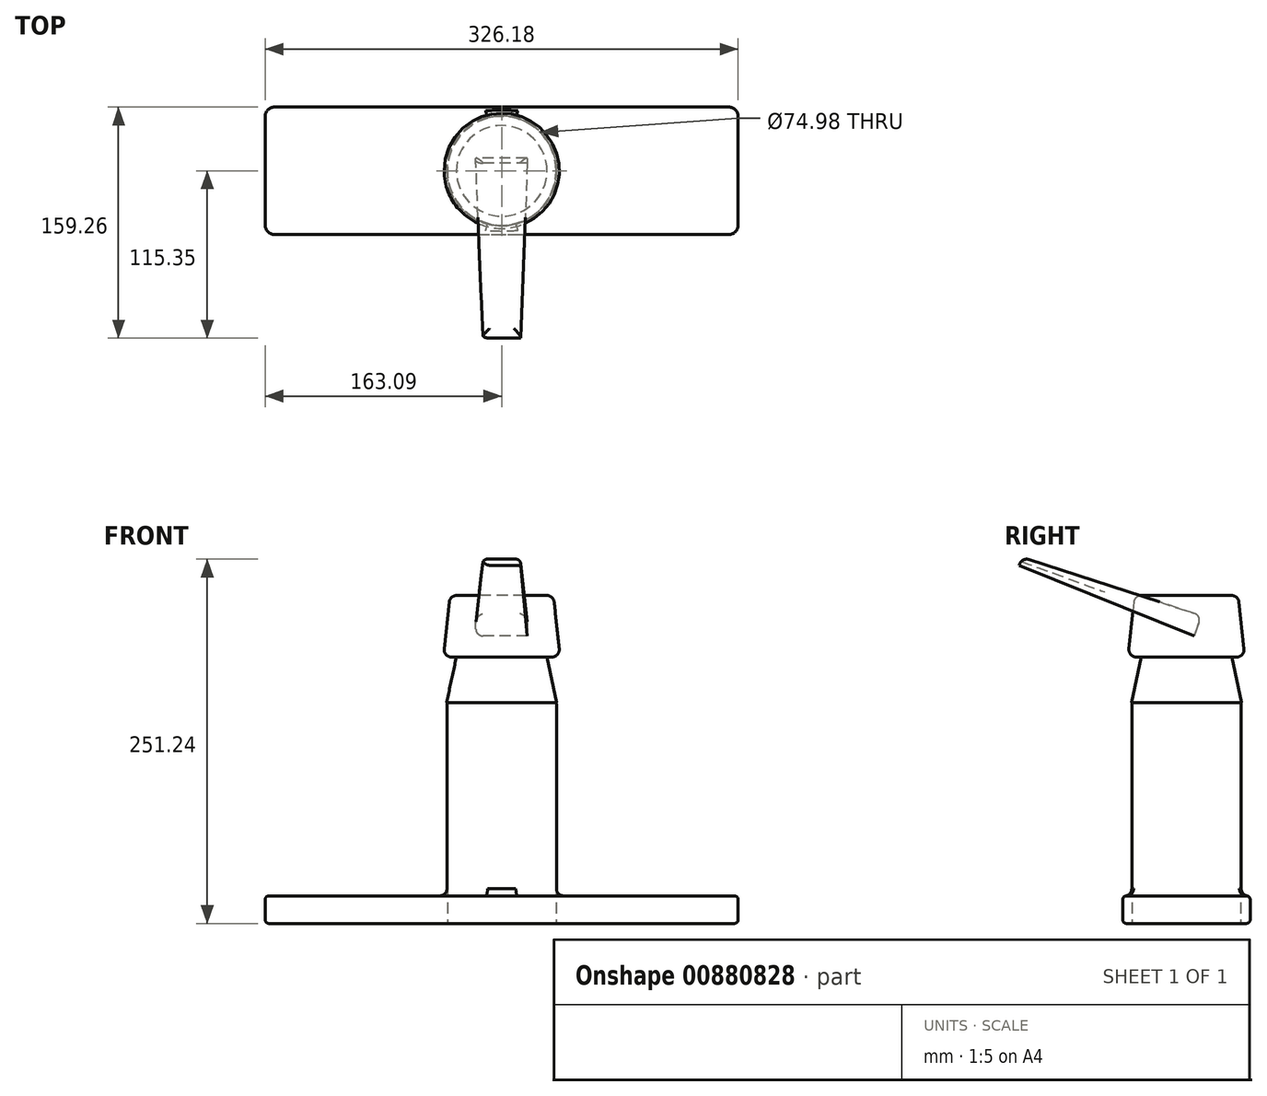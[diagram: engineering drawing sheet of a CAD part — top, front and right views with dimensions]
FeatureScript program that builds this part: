
annotation { "Feature Type Name" : "Feature", "Feature Type Description" : "" }
export const myFeature = defineFeature(function(context is Context, id is Id, definition is map)
    precondition{}
    {
        {
            var Q0;
            Q0=qCreatedBy(makeId("Top.planeOp"),FACE);
            var sketch = newSketch(context, id + "F0", { "sketchPlane" : qUnion([Q0])});
            skLineSegment(sketch, "E0.bottom", {"start": v(-156.74, 43.9) * mm, "end": v(156.74, 43.9) * mm});
            skLineSegment(sketch, "E0.top", {"start": v(-156.74, -43.9) * mm, "end": v(156.74, -43.9) * mm});
            skLineSegment(sketch, "E0.left", {"start": v(-163.09, 37.56) * mm, "end": v(-163.09, -37.56) * mm});
            skLineSegment(sketch, "E0.right", {"start": v(163.09, 37.56) * mm, "end": v(163.09, -37.56) * mm});
            skPoint(sketch, "E0.middle", {"position": v(0, 0) * mm});
            skCircle(sketch, "E1", {"center": v(0, 0) * mm, "radius": 37.74 * mm});
            skPoint(sketch, "E2.visualSharp", {"position": v(-163.09, 43.9) * mm});
            skArc(sketch, "E2.filletArc", {"start": v(-156.74, 43.9) * mm, "mid": v(-161.23, 42.05) * mm, "end": v(-163.09, 37.56) * mm});
            skLineSegment(sketch, "E3", {"start": v(-163.09, 0) * mm, "end": v(163.09, 0) * mm, "construction": true});
            skLineSegment(sketch, "E4", {"start": v(0, 43.9) * mm, "end": v(0, -43.9) * mm, "construction": true});
            skPoint(sketch, "E4.startSnap0", {"position": v(3.17, 43.9) * mm});
            skPoint(sketch, "E5.MirrorP", {"position": v(163.09, 43.9) * mm});
            skArc(sketch, "E6.filletArc", {"start": v(163.09, 37.56) * mm, "mid": v(161.23, 42.05) * mm, "end": v(156.74, 43.9) * mm});
            skPoint(sketch, "E7.visualSharp", {"position": v(-163.09, -43.9) * mm});
            skArc(sketch, "E7.filletArc", {"start": v(-163.09, -37.56) * mm, "mid": v(-161.23, -42.05) * mm, "end": v(-156.74, -43.9) * mm});
            skPoint(sketch, "E8.visualSharp", {"position": v(163.09, -43.9) * mm});
            skArc(sketch, "E8.filletArc", {"start": v(156.74, -43.9) * mm, "mid": v(161.23, -42.05) * mm, "end": v(163.09, -37.56) * mm});
            skSolve(sketch);
        }
        {
            var Q0;
            Q0=makeQuery(id+"F0.imprint","IMPRINT",FACE,{"disambiguationData":[TD([[makeQuery(id+"F0.imprint","IMPRINT",EDGE,{"derivedFrom":sQuery(id+"F0.wireOp",EDGE,"E1")}),1.0]])]});
            var Q1;
            Q1=sQuery(id+"F0.wireOp",EDGE,"E1");
            extrude(context, id + "F1", {"entities" : qUnion([Q0]), "bodyType" : ToolBodyType.SURFACE, "surfaceEntities" : qUnion([Q1]), "depth" : 38.1 * mm});
        }
        {
            var Q0;
            Q0=qSketchRegion(id+"F0",true);
            extrude(context, id + "F2", {"entities" : qUnion([Q0]), "depth" : 19.05 * mm});
        }
        {
            var Q0;
            Q0=makeQuery(id+"F2.opExtrude","CAP_FACE",FACE,{"disambiguationData":[OSD([sQuery(id+"F0.wireOp",EDGE,"E0.bottom"),sQuery(id+"F0.wireOp",EDGE,"E0.top"),sQuery(id+"F0.wireOp",EDGE,"E0.left"),sQuery(id+"F0.wireOp",EDGE,"E0.right"),sQuery(id+"F0.wireOp",EDGE,"E1"),sQuery(id+"F0.wireOp",EDGE,"E2.filletArc"),sQuery(id+"F0.wireOp",EDGE,"E6.filletArc"),sQuery(id+"F0.wireOp",EDGE,"E7.filletArc"),sQuery(id+"F0.wireOp",EDGE,"E8.filletArc")])],"isStart":false});
            var Q1;
            Q1=makeQuery(id+"F2.opExtrude","CAP_EDGE",EDGE,{"disambiguationData":[OSD([sQuery(id+"F0.wireOp",EDGE,"E0.top")])],"isStart":true});
            fillet(context, id + "F3", {"entities" : qUnion([Q0, Q1]), "radius" : 2.54 * mm, "tangentPropagation" : true, "allowEdgeOverflow" : false});
        }
        {
            var Q0;
            Q0=qCreatedBy(makeId("Top.planeOp"),FACE);
            var sketch = newSketch(context, id + "F4", { "sketchPlane" : qUnion([Q0])});
            skCircle(sketch, "E9", {"center": v(0, 0) * mm, "radius": 35.18 * mm});
            skSolve(sketch);
        }
        {
            var Q0;
            Q0=qSketchRegion(id+"F4",true);
            var Q1;
            Q1=qConstructionFilter(qBodyType(qCreatedBy(id+"F4",EDGE),BodyType.WIRE),ConstructionObject.NO);
            extrude(context, id + "F5", {"entities" : qUnion([Q0]), "bodyType" : ToolBodyType.SURFACE, "surfaceEntities" : qUnion([Q1]), "depth" : 127 * mm});
        }
        {
            var Q0;
            Q0=qCreatedBy(makeId("Top.planeOp"),FACE);
            var sketch = newSketch(context, id + "F6", { "sketchPlane" : qUnion([Q0])});
            skCircle(sketch, "E10.0", {"center": v(0, 0) * mm, "radius": 37.74 * mm});
            skCircle(sketch, "E11", {"center": v(0, 0) * mm, "radius": 37.5 * mm});
            skSolve(sketch);
        }
        {
            var Q0;
            Q0=qSketchRegion(id+"F6",true);
            extrude(context, id + "F7", {"entities" : qUnion([Q0]), "operationType" : NewBodyOperationType.ADD, "depth" : 152.4 * mm});
        }
        {
            var Q0;
            Q0=qCreatedBy(makeId("Front.planeOp"),FACE);
            var sketch = newSketch(context, id + "F8", { "sketchPlane" : qUnion([Q0])});
            skCircle(sketch, "E12", {"center": v(0, 79.78) * mm, "radius": 27.94 * mm});
            skSolve(sketch);
        }
        {
            var Q0;
            Q0=qSketchRegion(id+"F8",true);
            var Q1;
            Q1=sQuery(id+"F8.wireOp",EDGE,"E12");
            extrude(context, id + "F9", {"entities" : qUnion([Q0]), "bodyType" : ToolBodyType.SURFACE, "operationType" : NewBodyOperationType.ADD, "surfaceEntities" : qUnion([Q1]), "depth" : 101.6 * mm, "hasSecondDirection" : true, "secondDirectionOppositeDirection" : false, "secondDirectionDepth" : 18.8 * mm});
        }
        {
            var Q0;
            Q0=qCreatedBy(makeId("Front.planeOp"),FACE);
            var sketch = newSketch(context, id + "F10", { "sketchPlane" : qUnion([Q0])});
            skLineSegment(sketch, "E13", {"start": v(0, 0) * mm, "end": v(0, 151.68) * mm, "construction": true});
            skSolve(sketch);
        }
        {
            var Q0;
            Q0=qCreatedBy(makeId("Front.planeOp"),FACE);
            var sketch = newSketch(context, id + "F11", { "sketchPlane" : qUnion([Q0])});
            skLineSegment(sketch, "E14", {"start": v(38.11, 83.49) * mm, "end": v(-35, 83.49) * mm, "construction": true});
            skSolve(sketch);
        }
        {
            var Q0;
            Q0=makeQuery(id+"F9.opExtrude","SWEPT_BODY",BODY,{"disambiguationData":[OSD([sQuery(id+"F8.wireOp",EDGE,"E12")])]});
            var Q1;
            Q1=sQuery(id+"F11.wireOp",EDGE,"E14");
            transform(context, id + "F12", {"entities" : qUnion([Q0]), "transformType" : TransformType.ROTATION, "transformAxis" : qUnion([Q1]), "angle" : 20 * degree, "makeCopy" : false});
        }
        {
            var Q0;
            Q0=qCreatedBy(makeId("Front.planeOp"),FACE);
            var sketch = newSketch(context, id + "F13", { "sketchPlane" : qUnion([Q0])});
            skLineSegment(sketch, "E15", {"start": v(0, 152.43) * mm, "end": v(-38, 152.43) * mm});
            skLineSegment(sketch, "E16", {"start": v(-38, 152.43) * mm, "end": v(-27.76, 200.05) * mm});
            skLineSegment(sketch, "E17", {"start": v(-27.76, 200.05) * mm, "end": v(0, 200.05) * mm});
            skLineSegment(sketch, "E18", {"start": v(0, 200.05) * mm, "end": v(0, 152.43) * mm});
            skSolve(sketch);
        }
        {
            var Q0;
            Q0=makeQuery(id+"F13.imprint","IMPRINT",FACE,{"disambiguationData":[TD([[makeQuery(id+"F13.imprint","IMPRINT",EDGE,{"derivedFrom":sQuery(id+"F13.wireOp",EDGE,"E15")}),-1.0]])]});
            var Q1;
            Q1=sQuery(id+"F13.wireOp",EDGE,"E16");
            var Q2;
            Q2=sQuery(id+"F13.wireOp",EDGE,"E15");
            var Q3;
            Q3=sQuery(id+"F13.wireOp",EDGE,"E18");
            var Q4;
            Q4=sQuery(id+"F13.wireOp",EDGE,"E17");
            var Q5;
            Q5=sQuery(id+"F13.wireOp",EDGE,"E18");
            revolve(context, id + "F14", {"entities" : qUnion([Q0]), "surfaceEntities" : qUnion([Q1, Q2, Q3, Q4]), "axis" : qUnion([Q5]), "revolveType" : RevolveType.FULL});
        }
        {
            var Q0;
            Q0=qCreatedBy(makeId("Front.planeOp"),FACE);
            var sketch = newSketch(context, id + "F15", { "sketchPlane" : qUnion([Q0])});
            skLineSegment(sketch, "E19", {"start": v(0, 183.71) * mm, "end": v(-40.29, 183.71) * mm});
            skLineSegment(sketch, "E20", {"start": v(-40.29, 183.71) * mm, "end": v(-35.67, 226.23) * mm});
            skLineSegment(sketch, "E21", {"start": v(-35.67, 226.23) * mm, "end": v(0, 226.23) * mm});
            skLineSegment(sketch, "E22", {"start": v(0, 226.23) * mm, "end": v(0, 183.71) * mm});
            skSolve(sketch);
        }
        {
            var Q0;
            Q0=makeQuery(id+"F15.imprint","IMPRINT",FACE,{"disambiguationData":[TD([[makeQuery(id+"F15.imprint","IMPRINT",EDGE,{"derivedFrom":sQuery(id+"F15.wireOp",EDGE,"E19")}),-1.0]])]});
            var Q1;
            Q1=sQuery(id+"F10.wireOp",EDGE,"E13");
            revolve(context, id + "F16", {"operationType" : NewBodyOperationType.ADD, "entities" : qUnion([Q0]), "axis" : qUnion([Q1]), "revolveType" : RevolveType.FULL});
        }
        {
            var Q0;
            Q0=qCreatedBy(makeId("Front.planeOp"),FACE);
            var sketch = newSketch(context, id + "F17", { "sketchPlane" : qUnion([Q0])});
            skLineSegment(sketch, "E23.bottom", {"start": v(-17.84, 214.13) * mm, "end": v(17.66, 214.13) * mm});
            skLineSegment(sketch, "E23.top", {"start": v(-17.84, 199.2) * mm, "end": v(17.66, 199.2) * mm});
            skLineSegment(sketch, "E23.left", {"start": v(-17.84, 214.13) * mm, "end": v(-17.84, 199.2) * mm});
            skLineSegment(sketch, "E23.right", {"start": v(17.66, 214.13) * mm, "end": v(17.66, 199.2) * mm});
            skLineSegment(sketch, "E24", {"start": v(-17.84, 206.67) * mm, "end": v(17.66, 206.67) * mm, "construction": true});
            skSolve(sketch);
        }
        {
            var Q0;
            Q0=qSketchRegion(id+"F17",true);
            extrude(context, id + "F18", {"entities" : qUnion([Q0]), "depth" : 130.05 * mm, "hasDraft" : true, "draftAngle" : 2 * degree, "draftPullDirection" : true});
        }
        {
            var Q0;
            Q0=makeQuery(id+"F18.opExtrude","SWEPT_BODY",BODY,{"disambiguationData":[OSD([sQuery(id+"F17.wireOp",EDGE,"E23.bottom"),sQuery(id+"F17.wireOp",EDGE,"E23.top"),sQuery(id+"F17.wireOp",EDGE,"E23.left"),sQuery(id+"F17.wireOp",EDGE,"E23.right")])]});
            var Q1;
            Q1=sQuery(id+"F15.wireOp",EDGE,"E19");
            transform(context, id + "F19", {"entities" : qUnion([Q0]), "transformType" : TransformType.ROTATION, "transformAxis" : qUnion([Q1]), "angle" : 20 * degree, "makeCopy" : false});
        }
        {
            var Q0;
            Q0=qCreatedBy(makeId("Right.planeOp"),FACE);
            var sketch = newSketch(context, id + "F20", { "sketchPlane" : qUnion([Q0])});
            skLineSegment(sketch, "E25", {"start": v(0, 0) * mm, "end": v(-120.43, 0) * mm});
            skLineSegment(sketch, "E26", {"start": v(-120.43, 0) * mm, "end": v(0, 0) * mm});
            skLineSegment(sketch, "E27", {"start": v(0, 0) * mm, "end": v(-36.67, -100.75) * mm});
            skSolve(sketch);
        }
        {
            var Q0;
            Q0=qCreatedBy(makeId("Front.planeOp"),FACE);
            var Q1;
            Q1=sQuery(id+"F20.wireOp",EDGE,"E27");
            cPlane(context, id + "F21", {"entities" : qUnion([Q0, Q1]), "cplaneType" : CPlaneType.LINE_ANGLE, "offset" : 25.4 * mm, "angle" : 0 * degree, "width" : 152.4 * mm, "height" : 152.4 * mm});
        }
        {
            var Q0;
            Q0=qCreatedBy(id+"F21.planeOp",FACE);
            cPlane(context, id + "F22", {"entities" : qUnion([Q0]), "cplaneType" : CPlaneType.OFFSET, "offset" : 98.55 * mm, "oppositeDirection" : true, "width" : 152.4 * mm, "height" : 152.4 * mm});
        }
        {
            var Q0;
            Q0=qCreatedBy(id+"F22.planeOp",FACE);
            var sketch = newSketch(context, id + "F23", { "sketchPlane" : qUnion([Q0])});
            skCircle(sketch, "E28", {"center": v(0, 75.31) * mm, "radius": 26.5 * mm});
            skSolve(sketch);
        }
        {
            var Q0;
            Q0=qCreatedBy(makeId("Right.planeOp"),FACE);
            var sketch = newSketch(context, id + "F24", { "sketchPlane" : qUnion([Q0])});
            skFitSpline(sketch, "E29", {"points": [v(-30.34, 87.73) * mm, v(-170.12, 135.42) * mm, v(-249.59, 136.95) * mm], "startDerivative": vector(-291.12, 163.3) * mm, "endDerivative": vector(-240.6, -23.16) * mm});
            skSolve(sketch);
        }
        {
            var Q0;
            Q0=qSketchRegion(id+"F23",true);
            var Q1;
            Q1=sQuery(id+"F23.wireOp",EDGE,"E28");
            var Q2;
            Q2=sQuery(id+"F24.wireOp",EDGE,"otEZL0sl-9XYc-qNy6-Q2Yl-TIyQWOSTfNdC");
            var Q3;
            Q3=sQuery(id+"F24.wireOp",EDGE,"E29");
            sweep(context, id + "F25", {"bodyType" : ToolBodyType.SURFACE, "profiles" : qUnion([Q0]), "surfaceProfiles" : qUnion([Q1, Q2]), "path" : qUnion([Q3])});
        }
        {
            var Q0;
            Q0=qCreatedBy(makeId("Right.planeOp"),FACE);
            var sketch = newSketch(context, id + "F26", { "sketchPlane" : qUnion([Q0])});
            skLineSegment(sketch, "E30", {"start": v(-302.37, 169.55) * mm, "end": v(-280.41, 169.55) * mm});
            skLineSegment(sketch, "E31", {"start": v(-280.41, 169.55) * mm, "end": v(-265.4, 149.32) * mm});
            skLineSegment(sketch, "E32", {"start": v(-265.4, 149.32) * mm, "end": v(-265.4, 88.07) * mm});
            skLineSegment(sketch, "E33", {"start": v(-265.4, 88.07) * mm, "end": v(-301.8, 88.07) * mm});
            skLineSegment(sketch, "E34", {"start": v(-301.8, 88.07) * mm, "end": v(-302.37, 169.55) * mm});
            skSolve(sketch);
        }
        {
            var Q0;
            Q0=sQuery(id+"F26.wireOp",EDGE,"E32");
            var Q1;
            Q1=sQuery(id+"F26.wireOp",EDGE,"E31");
            var Q2;
            Q2=sQuery(id+"F26.wireOp",EDGE,"E30");
            var Q3;
            Q3=sQuery(id+"F26.wireOp",EDGE,"E33");
            var Q4;
            Q4=sQuery(id+"F26.wireOp",EDGE,"E34");
            revolve(context, id + "F27", {"bodyType" : ToolBodyType.SURFACE, "surfaceEntities" : qUnion([Q0, Q1, Q2, Q3]), "axis" : qUnion([Q4]), "revolveType" : RevolveType.FULL});
        }
        {
            var Q0;
            Q0=makeQuery(id+"F27.opRevolve","SWEPT_EDGE",EDGE,{"disambiguationData":[OSD([sQuery(id+"F26.wireOp",VERTEX,"E30.end")])]});
            fillet(context, id + "F28", {"entities" : qUnion([Q0]), "radius" : 0.08 * mm, "tangentPropagation" : true, "allowEdgeOverflow" : false});
        }
        {
            var Q0;
            Q0=makeQuery(id+"F18.opExtrude","SWEPT_FACE",FACE,{"disambiguationData":[OSD([sQuery(id+"F17.wireOp",EDGE,"E23.bottom")])]});
            var Q1;
            Q1=makeQuery(id+"F18.opExtrude","SWEPT_EDGE",EDGE,{"disambiguationData":[OSD([sQuery(id+"F17.wireOp",EDGE,"E23.top"),sQuery(id+"F17.wireOp",EDGE,"E23.left")])]});
            fillet(context, id + "F29", {"entities" : qUnion([Q0, Q1]), "radius" : 5.08 * mm, "tangentPropagation" : true, "allowEdgeOverflow" : false});
        }
        {
            var Q0;
            Q0=makeQuery(id+"F16.opRevolve","SWEPT_FACE",FACE,{"disambiguationData":[OSD([sQuery(id+"F15.wireOp",EDGE,"E21")])]});
            var Q1;
            Q1=makeQuery(id+"F16.opRevolve","SWEPT_FACE",FACE,{"disambiguationData":[OSD([sQuery(id+"F15.wireOp",EDGE,"E20")])]});
            fillet(context, id + "F30", {"entities" : qUnion([Q0, Q1]), "radius" : 5.08 * mm, "tangentPropagation" : true, "allowEdgeOverflow" : false});
        }
        {
            var Q0;
            Q0=makeQuery(id+"F27.opRevolve","SWEPT_FACE",FACE,{"disambiguationData":[OSD([sQuery(id+"F26.wireOp",EDGE,"E30")])]});
            var Q1;
            Q1=makeQuery(id+"F27.opRevolve","SWEPT_FACE",FACE,{"disambiguationData":[OSD([sQuery(id+"F26.wireOp",EDGE,"E31")])]});
            var Q2;
            Q2=makeQuery(id+"F27.opRevolve","SWEPT_FACE",FACE,{"disambiguationData":[OSD([sQuery(id+"F26.wireOp",EDGE,"E32")])]});
            fillet(context, id + "F31", {"entities" : qUnion([Q0, Q1, Q2]), "radius" : 5.08 * mm, "tangentPropagation" : true, "allowEdgeOverflow" : false});
        }
        {
            var Q0;
            Q0=makeQuery(id+"F7.opExtrude","SWEPT_FACE",FACE,{"disambiguationData":[OSD([sQuery(id+"F6.wireOp",EDGE,"E10.0")])]});
            var Q1;
            Q1=makeQuery(id+"F1.opExtrude","SWEPT_FACE",FACE,{"disambiguationData":[OSD([sQuery(id+"F0.wireOp",EDGE,"E1")])]});
            fillet(context, id + "F32", {"entities" : qUnion([Q0, Q1]), "radius" : 5.08 * mm, "tangentPropagation" : true, "allowEdgeOverflow" : false});
        }
    });
